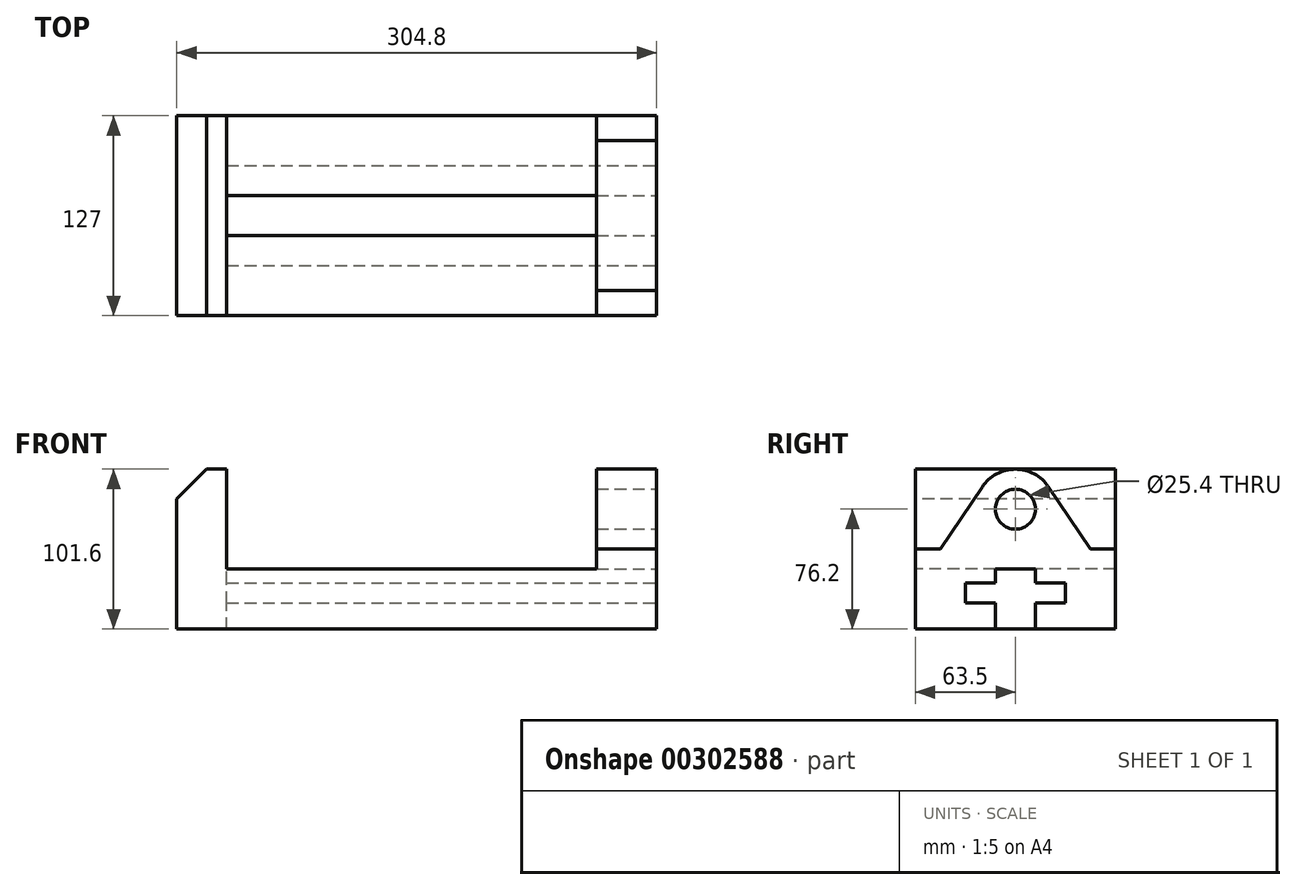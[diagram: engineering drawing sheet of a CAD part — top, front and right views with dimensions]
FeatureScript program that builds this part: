
annotation { "Feature Type Name" : "Feature", "Feature Type Description" : "" }
export const myFeature = defineFeature(function(context is Context, id is Id, definition is map)
    precondition{}
    {
        {
            var Q0;
            Q0=qCreatedBy(makeId("Front.planeOp"),FACE);
            var sketch = newSketch(context, id + "F0", { "sketchPlane" : qUnion([Q0])});
            skLineSegment(sketch, "E0.bottom", {"start": v(0, 0) * mm, "end": v(0, 0) * mm});
            skLineSegment(sketch, "E1", {"start": v(19.05, 101.6) * mm, "end": v(31.75, 101.6) * mm});
            skLineSegment(sketch, "E2", {"start": v(31.75, 101.6) * mm, "end": v(31.75, 38.1) * mm});
            skLineSegment(sketch, "E3", {"start": v(31.75, 38.1) * mm, "end": v(266.7, 38.1) * mm});
            skLineSegment(sketch, "E4", {"start": v(266.7, 38.1) * mm, "end": v(266.7, 101.6) * mm});
            skLineSegment(sketch, "E5", {"start": v(266.7, 101.6) * mm, "end": v(304.8, 101.6) * mm});
            skLineSegment(sketch, "E6", {"start": v(304.8, 101.6) * mm, "end": v(304.8, 0) * mm});
            skLineSegment(sketch, "E7", {"start": v(304.8, 0) * mm, "end": v(0, 0) * mm});
            skLineSegment(sketch, "E8", {"start": v(0, 0) * mm, "end": v(0, 82.55) * mm});
            skLineSegment(sketch, "E9", {"start": v(0, 82.55) * mm, "end": v(19.05, 101.6) * mm});
            skLineSegment(sketch, "E10", {"start": v(0, 82.55) * mm, "end": v(19.05, 82.55) * mm, "construction": true});
            skLineSegment(sketch, "E11", {"start": v(19.05, 82.55) * mm, "end": v(19.05, 101.6) * mm, "construction": true});
            skSolve(sketch);
        }
        {
            var Q0;
            Q0=makeQuery(id+"F0.imprint","IMPRINT",FACE,{"disambiguationData":[TD([[makeQuery(id+"F0.imprint","IMPRINT",EDGE,{"derivedFrom":sQuery(id+"F0.wireOp",EDGE,"E1")}),-1.0]])]});
            extrude(context, id + "F1", {"entities" : qUnion([Q0]), "oppositeDirection" : true, "depth" : 127 * mm});
        }
        {
            var Q0;
            Q0=makeQuery(id+"F1.opExtrude","SWEPT_FACE",FACE,{"disambiguationData":[OSD([sQuery(id+"F0.wireOp",EDGE,"E6")])]});
            var sketch = newSketch(context, id + "F2", { "sketchPlane" : qUnion([Q0])});
            skLineSegment(sketch, "E12", {"start": v(0, 50.8) * mm, "end": v(15.88, 50.8) * mm});
            skLineSegment(sketch, "E13", {"start": v(15.87, 50.8) * mm, "end": v(42.4, 90.35) * mm});
            skLineSegment(sketch, "E14", {"start": v(84.6, 90.35) * mm, "end": v(111.13, 50.8) * mm});
            skLineSegment(sketch, "E15", {"start": v(111.13, 50.8) * mm, "end": v(127, 50.8) * mm});
            skLineSegment(sketch, "E16", {"start": v(127, 50.8) * mm, "end": v(127, 0) * mm});
            skLineSegment(sketch, "E17", {"start": v(127, 0) * mm, "end": v(0, 0) * mm});
            skLineSegment(sketch, "E18", {"start": v(0, 0) * mm, "end": v(0, 50.8) * mm});
            skArc(sketch, "E19", {"start": v(84.6, 90.35) * mm, "mid": v(63.5, 101.6) * mm, "end": v(42.4, 90.35) * mm});
            skCircle(sketch, "E20", {"center": v(63.5, 76.2) * mm, "radius": 12.7 * mm});
            skLineSegment(sketch, "E21", {"start": v(63.5, 0) * mm, "end": v(63.5, 104.45) * mm, "construction": true});
            skLineSegment(sketch, "E22", {"start": v(50.8, 0) * mm, "end": v(50.8, 16.51) * mm});
            skLineSegment(sketch, "E23", {"start": v(50.8, 16.51) * mm, "end": v(31.75, 16.51) * mm});
            skLineSegment(sketch, "E24", {"start": v(31.75, 16.51) * mm, "end": v(31.75, 29.2) * mm});
            skLineSegment(sketch, "E25", {"start": v(31.75, 29.2) * mm, "end": v(50.8, 29.21) * mm});
            skLineSegment(sketch, "E26", {"start": v(50.8, 29.21) * mm, "end": v(50.8, 38.1) * mm});
            skLineSegment(sketch, "E27", {"start": v(50.8, 38.1) * mm, "end": v(63.5, 38.1) * mm});
            skLineSegment(sketch, "E28", {"start": v(63.5, 38.1) * mm, "end": v(76.2, 38.1) * mm});
            skLineSegment(sketch, "E29", {"start": v(76.2, 38.1) * mm, "end": v(76.2, 29.21) * mm});
            skLineSegment(sketch, "E30", {"start": v(76.2, 29.21) * mm, "end": v(95.25, 29.21) * mm});
            skLineSegment(sketch, "E31", {"start": v(95.25, 29.21) * mm, "end": v(95.25, 16.51) * mm});
            skLineSegment(sketch, "E32", {"start": v(95.25, 16.51) * mm, "end": v(76.2, 16.51) * mm});
            skLineSegment(sketch, "E33", {"start": v(76.2, 16.51) * mm, "end": v(76.2, 0) * mm});
            skLineSegment(sketch, "E34", {"start": v(76.2, 0) * mm, "end": v(50.8, 0) * mm});
            skSolve(sketch);
        }
        {
            var Q0;
            {var subQ4=sQuery(id+"F2.wireOp",EDGE,"E12");Q0=makeQuery(id+"F2.imprint","IMPRINT",FACE,{"disambiguationData":[TD([[makeQuery(id+"F2.imprint","IMPRINT",EDGE,{"derivedFrom":subQ4}),1.0]])]});}
            var Q1;
            {var subQ6=sQuery(id+"F2.wireOp",EDGE,"E14");Q1=makeQuery(id+"F2.imprint","IMPRINT",FACE,{"disambiguationData":[TD([[makeQuery(id+"F2.imprint","IMPRINT",EDGE,{"derivedFrom":subQ6}),1.0]])]});}
            extrude(context, id + "F3", {"entities" : qUnion([Q0, Q1]), "operationType" : NewBodyOperationType.REMOVE, "oppositeDirection" : true, "depth" : 38.1 * mm});
        }
        {
            var Q0;
            Q0=makeQuery(id+"F2.imprint","IMPRINT",FACE,{"disambiguationData":[TD([[makeQuery(id+"F2.imprint","IMPRINT",EDGE,{"derivedFrom":sQuery(id+"F2.wireOp",EDGE,"E22")}),-1.0]])]});
            extrude(context, id + "F4", {"entities" : qUnion([Q0]), "operationType" : NewBodyOperationType.REMOVE, "oppositeDirection" : true, "depth" : 273.05 * mm});
        }
        {
            var Q0;
            Q0=makeQuery(id+"F2.imprint","IMPRINT",FACE,{"disambiguationData":[TD([[makeQuery(id+"F2.imprint","IMPRINT",EDGE,{"derivedFrom":sQuery(id+"F2.wireOp",EDGE,"E20")}),1.0]])]});
            extrude(context, id + "F5", {"entities" : qUnion([Q0]), "operationType" : NewBodyOperationType.REMOVE, "oppositeDirection" : true, "depth" : 38.1 * mm});
        }
    });
